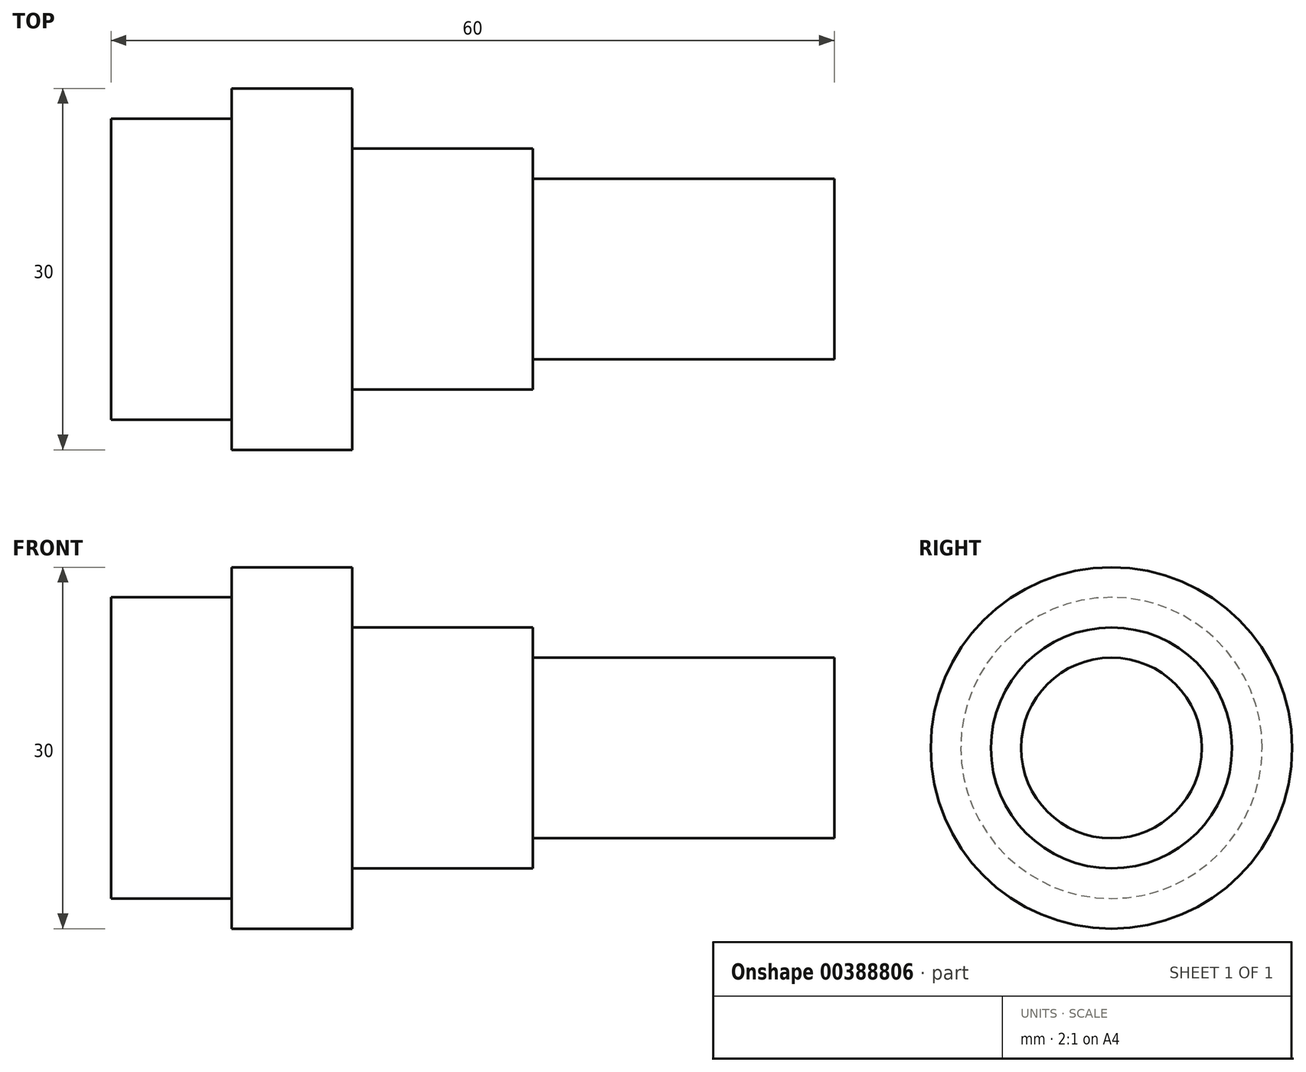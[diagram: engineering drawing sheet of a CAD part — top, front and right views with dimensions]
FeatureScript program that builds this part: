
annotation { "Feature Type Name" : "Feature", "Feature Type Description" : "" }
export const myFeature = defineFeature(function(context is Context, id is Id, definition is map)
    precondition{}
    {
        {
            var Q0;
            Q0=qCreatedBy(makeId("Front.planeOp"),FACE);
            var sketch = newSketch(context, id + "F0", { "sketchPlane" : qUnion([Q0])});
            skLineSegment(sketch, "E0", {"start": v(0, 0) * mm, "end": v(0, 7.5) * mm});
            skLineSegment(sketch, "E1", {"start": v(0, 7.5) * mm, "end": v(-25, 7.5) * mm});
            skLineSegment(sketch, "E2", {"start": v(-25, 7.5) * mm, "end": v(-25, 10) * mm});
            skLineSegment(sketch, "E3", {"start": v(-25, 10) * mm, "end": v(-40, 10) * mm});
            skLineSegment(sketch, "E4", {"start": v(-40, 10) * mm, "end": v(-40, 15) * mm});
            skLineSegment(sketch, "E5", {"start": v(-40, 15) * mm, "end": v(-50, 15) * mm});
            skLineSegment(sketch, "E6", {"start": v(-50, 12.5) * mm, "end": v(-50, 15) * mm});
            skLineSegment(sketch, "E7", {"start": v(-50, 12.5) * mm, "end": v(-60, 12.5) * mm});
            skLineSegment(sketch, "E8", {"start": v(0, 0) * mm, "end": v(-76.2, 0) * mm, "construction": true});
            skLineSegment(sketch, "E9", {"start": v(-60, 12.5) * mm, "end": v(-60, 0) * mm});
            skLineSegment(sketch, "E10", {"start": v(-60, 0) * mm, "end": v(0, 0) * mm});
            skSolve(sketch);
        }
        {
            var Q0;
            Q0 = qSketchRegion(id + "F0", true);
            var Q1;
            Q1=sQuery(id+"F0.wireOp",EDGE,"E10");
            revolve(context, id + "F1", {"entities" : qUnion([Q0]), "axis" : qUnion([Q1]), "revolveType" : RevolveType.FULL});
        }
    });
